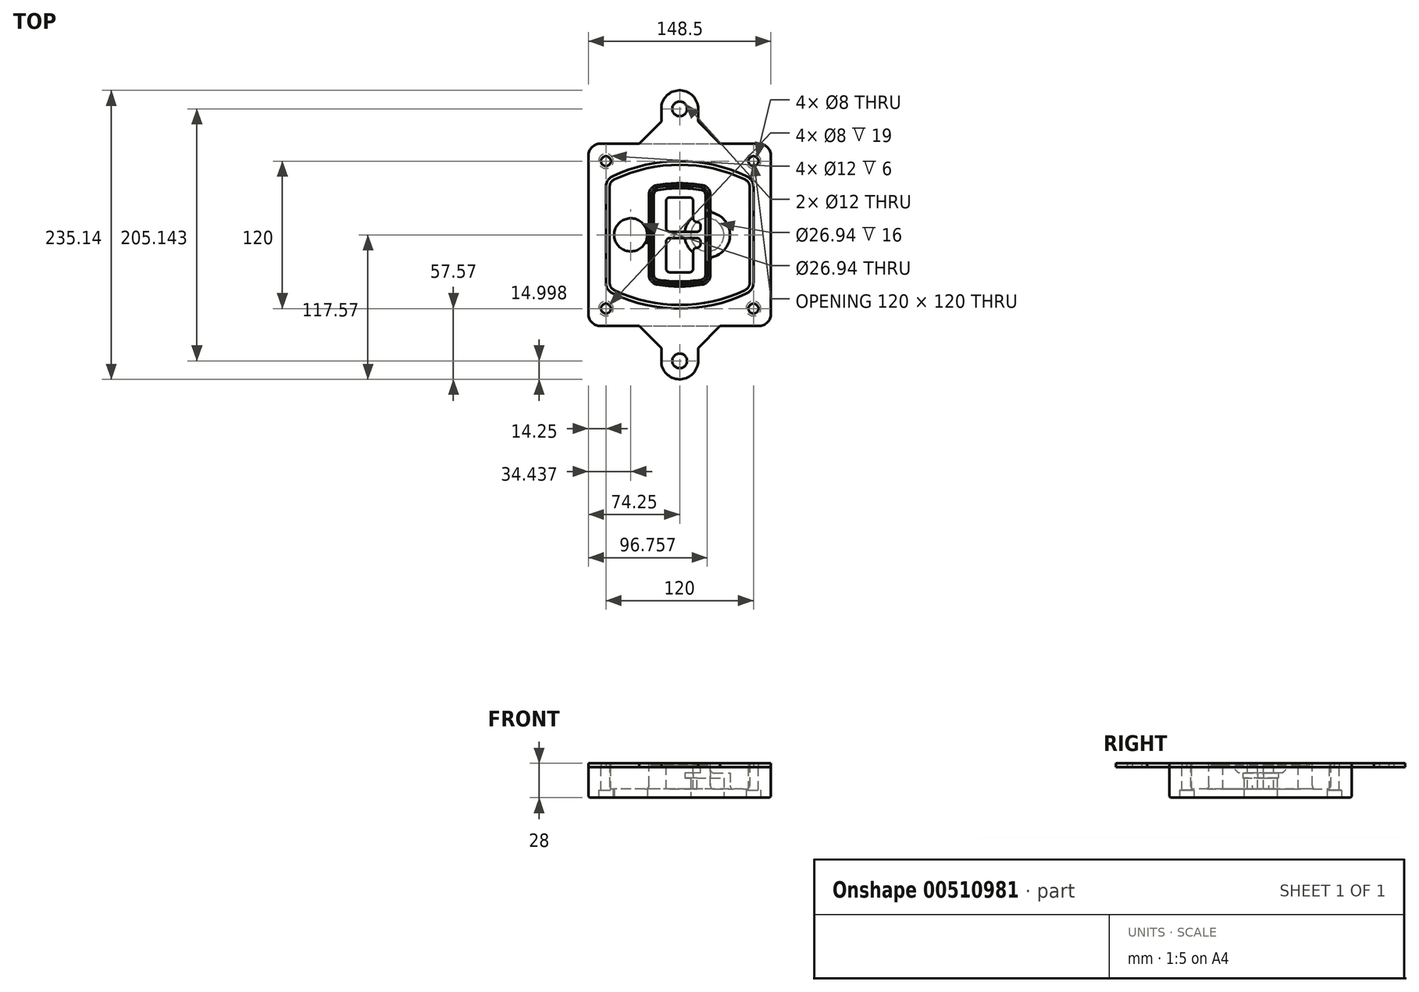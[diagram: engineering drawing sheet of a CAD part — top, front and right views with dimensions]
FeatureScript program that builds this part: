
annotation { "Feature Type Name" : "Feature", "Feature Type Description" : "" }
export const myFeature = defineFeature(function(context is Context, id is Id, definition is map)
    precondition{}
    {
        {
            var Q0;
            Q0=qCreatedBy(makeId("Top.planeOp"),FACE);
            var sketch = newSketch(context, id + "F0", { "sketchPlane" : qUnion([Q0])});
            skPoint(sketch, "E0.rect.middle", {"position": v(0, 0) * mm});
            skLineSegment(sketch, "E1.bottom", {"start": v(-64.25, -74.25) * mm, "end": v(64.25, -74.25) * mm});
            skLineSegment(sketch, "E1.top", {"start": v(-64.25, 74.25) * mm, "end": v(64.25, 74.25) * mm});
            skLineSegment(sketch, "E1.left", {"start": v(-74.25, -64.25) * mm, "end": v(-74.25, 64.25) * mm});
            skLineSegment(sketch, "E1.right", {"start": v(74.25, -64.25) * mm, "end": v(74.25, 64.25) * mm});
            skLineSegment(sketch, "E2", {"start": v(-74.25, 74.25) * mm, "end": v(74.25, -74.25) * mm, "construction": true});
            skLineSegment(sketch, "E3", {"start": v(74.25, 74.25) * mm, "end": v(-74.25, -74.25) * mm, "construction": true});
            skCircle(sketch, "E4", {"center": v(-60, 60) * mm, "radius": 4 * mm});
            skCircle(sketch, "E5", {"center": v(60, 60) * mm, "radius": 4 * mm});
            skCircle(sketch, "E6", {"center": v(60, -60) * mm, "radius": 4 * mm});
            skCircle(sketch, "E7", {"center": v(-60, -60) * mm, "radius": 4 * mm});
            skLineSegment(sketch, "E8", {"start": v(-60, 60) * mm, "end": v(60, 60) * mm, "construction": true});
            skLineSegment(sketch, "E9", {"start": v(60, 60) * mm, "end": v(60, -60) * mm, "construction": true});
            skLineSegment(sketch, "E10", {"start": v(60, -60) * mm, "end": v(-60, -60) * mm, "construction": true});
            skLineSegment(sketch, "E11", {"start": v(-60, -60) * mm, "end": v(-60, 60) * mm, "construction": true});
            skLineSegment(sketch, "E12", {"start": v(-60, 38.83) * mm, "end": v(-60, -38.83) * mm});
            skLineSegment(sketch, "E13", {"start": v(60, 38.83) * mm, "end": v(60, -38.83) * mm});
            skArc(sketch, "E14", {"start": v(54.26, 47.88) * mm, "mid": v(0, 60) * mm, "end": v(-54.26, 47.88) * mm});
            skArc(sketch, "E15", {"start": v(-54.26, -47.88) * mm, "mid": v(0, -60) * mm, "end": v(54.26, -47.88) * mm});
            skLineSegment(sketch, "E16", {"start": v(-60, 0) * mm, "end": v(60, 0) * mm, "construction": true});
            skPoint(sketch, "E17.visualSharp", {"position": v(-60, -45) * mm});
            skArc(sketch, "E17.filletArc", {"start": v(-60, -38.83) * mm, "mid": v(-58.44, -44.2) * mm, "end": v(-54.26, -47.88) * mm});
            skPoint(sketch, "E18.visualSharp", {"position": v(-60, 45) * mm});
            skArc(sketch, "E18.filletArc", {"start": v(-54.26, 47.88) * mm, "mid": v(-58.44, 44.2) * mm, "end": v(-60, 38.83) * mm});
            skPoint(sketch, "E19.visualSharp", {"position": v(60, 45) * mm});
            skArc(sketch, "E19.filletArc", {"start": v(60, 38.83) * mm, "mid": v(58.44, 44.2) * mm, "end": v(54.26, 47.88) * mm});
            skPoint(sketch, "E20.visualSharp", {"position": v(60, -45) * mm});
            skArc(sketch, "E20.filletArc", {"start": v(54.26, -47.88) * mm, "mid": v(58.44, -44.2) * mm, "end": v(60, -38.83) * mm});
            skPoint(sketch, "E21.visualSharp", {"position": v(-74.25, 74.25) * mm});
            skArc(sketch, "E21.filletArc", {"start": v(-64.25, 74.25) * mm, "mid": v(-71.32, 71.32) * mm, "end": v(-74.25, 64.25) * mm});
            skPoint(sketch, "E22.visualSharp", {"position": v(74.25, 74.25) * mm});
            skArc(sketch, "E22.filletArc", {"start": v(74.25, 64.25) * mm, "mid": v(71.32, 71.32) * mm, "end": v(64.25, 74.25) * mm});
            skPoint(sketch, "E23.visualSharp", {"position": v(74.25, -74.25) * mm});
            skArc(sketch, "E23.filletArc", {"start": v(64.25, -74.25) * mm, "mid": v(71.32, -71.32) * mm, "end": v(74.25, -64.25) * mm});
            skPoint(sketch, "E24.visualSharp", {"position": v(-74.25, -74.25) * mm});
            skArc(sketch, "E24.filletArc", {"start": v(-74.25, -64.25) * mm, "mid": v(-71.32, -71.32) * mm, "end": v(-64.25, -74.25) * mm});
            skArc(sketch, "E25.0", {"start": v(57, 38.83) * mm, "mid": v(55.9, 42.58) * mm, "end": v(52.98, 45.17) * mm});
            skLineSegment(sketch, "E25.1", {"start": v(57, 38.83) * mm, "end": v(57, -38.83) * mm});
            skArc(sketch, "E25.2", {"start": v(52.98, -45.17) * mm, "mid": v(55.9, -42.58) * mm, "end": v(57, -38.83) * mm});
            skArc(sketch, "E25.3", {"start": v(-52.98, -45.17) * mm, "mid": v(0, -57) * mm, "end": v(52.98, -45.17) * mm});
            skArc(sketch, "E25.4", {"start": v(-57, -38.83) * mm, "mid": v(-55.9, -42.58) * mm, "end": v(-52.98, -45.17) * mm});
            skArc(sketch, "E25.5", {"start": v(52.98, 45.17) * mm, "mid": v(0, 57) * mm, "end": v(-52.98, 45.17) * mm});
            skLineSegment(sketch, "E25.6", {"start": v(-57, 38.83) * mm, "end": v(-57, -38.83) * mm});
            skArc(sketch, "E25.7", {"start": v(-52.98, 45.17) * mm, "mid": v(-55.9, 42.58) * mm, "end": v(-57, 38.83) * mm});
            skArc(sketch, "E26.0", {"start": v(-55.96, 51.5) * mm, "mid": v(-61.82, 46.33) * mm, "end": v(-64, 38.83) * mm});
            skArc(sketch, "E26.1", {"start": v(55.96, 51.5) * mm, "mid": v(0, 64) * mm, "end": v(-55.96, 51.5) * mm});
            skArc(sketch, "E26.2", {"start": v(64, 38.83) * mm, "mid": v(61.82, 46.33) * mm, "end": v(55.96, 51.5) * mm});
            skLineSegment(sketch, "E26.3", {"start": v(64, 38.83) * mm, "end": v(64, -38.83) * mm});
            skArc(sketch, "E26.4", {"start": v(55.96, -51.5) * mm, "mid": v(61.82, -46.33) * mm, "end": v(64, -38.83) * mm});
            skLineSegment(sketch, "E26.5", {"start": v(-64, 38.83) * mm, "end": v(-64, -38.83) * mm});
            skArc(sketch, "E26.6", {"start": v(-55.96, -51.5) * mm, "mid": v(0, -64) * mm, "end": v(55.96, -51.5) * mm});
            skArc(sketch, "E26.7", {"start": v(-64, -38.83) * mm, "mid": v(-61.82, -46.33) * mm, "end": v(-55.96, -51.5) * mm});
            skSolve(sketch);
        }
        {
            var Q0;
            Q0=makeQuery(id+"F0.imprint","IMPRINT",FACE,{"disambiguationData":[TD([[makeQuery(id+"F0.imprint","IMPRINT",EDGE,{"derivedFrom":sQuery(id+"F0.wireOp",EDGE,"E1.bottom")}),1.0]])]});
            var Q1;
            Q1=makeQuery(id+"F0.imprint","IMPRINT",FACE,{"disambiguationData":[TD([[makeQuery(id+"F0.imprint","IMPRINT",EDGE,{"derivedFrom":sQuery(id+"F0.wireOp",EDGE,"E12")}),1.0]])]});
            var Q2;
            Q2=makeQuery(id+"F0.imprint","IMPRINT",FACE,{"disambiguationData":[TD([[makeQuery(id+"F0.imprint","IMPRINT",EDGE,{"derivedFrom":sQuery(id+"F0.wireOp",EDGE,"E25.0")}),1.0]])]});
            var Q3;
            Q3=makeQuery(id+"F0.imprint","IMPRINT",FACE,{"disambiguationData":[TD([[makeQuery(id+"F0.imprint","IMPRINT",EDGE,{"derivedFrom":sQuery(id+"F0.wireOp",EDGE,"E12")}),-1.0]])]});
            extrude(context, id + "F1", {"entities" : qUnion([Q0, Q1, Q2, Q3]), "oppositeDirection" : true, "depth" : 25 * mm});
        }
        {
            var Q0;
            Q0=makeQuery(id+"F0.imprint","IMPRINT",FACE,{"disambiguationData":[TD([[makeQuery(id+"F0.imprint","IMPRINT",EDGE,{"derivedFrom":sQuery(id+"F0.wireOp",EDGE,"E12")}),1.0]])]});
            extrude(context, id + "F2", {"entities" : qUnion([Q0]), "operationType" : NewBodyOperationType.ADD, "depth" : 3 * mm});
        }
        {
            var Q0;
            Q0=makeQuery(id+"F0.imprint","IMPRINT",FACE,{"disambiguationData":[TD([[makeQuery(id+"F0.imprint","IMPRINT",EDGE,{"derivedFrom":sQuery(id+"F0.wireOp",EDGE,"E25.0")}),1.0]])]});
            extrude(context, id + "F3", {"entities" : qUnion([Q0]), "operationType" : NewBodyOperationType.REMOVE, "oppositeDirection" : true, "depth" : 18 * mm});
        }
        {
            var Q0;
            Q0=makeQuery(id+"F2.opExtrude","CAP_FACE",FACE,{"disambiguationData":[OSD([sQuery(id+"F0.wireOp",EDGE,"E12"),sQuery(id+"F0.wireOp",EDGE,"E13"),sQuery(id+"F0.wireOp",EDGE,"E14"),sQuery(id+"F0.wireOp",EDGE,"E15"),sQuery(id+"F0.wireOp",EDGE,"E17.filletArc"),sQuery(id+"F0.wireOp",EDGE,"E18.filletArc"),sQuery(id+"F0.wireOp",EDGE,"E19.filletArc"),sQuery(id+"F0.wireOp",EDGE,"E20.filletArc"),sQuery(id+"F0.wireOp",EDGE,"E25.0"),sQuery(id+"F0.wireOp",EDGE,"E25.1"),sQuery(id+"F0.wireOp",EDGE,"E25.2"),sQuery(id+"F0.wireOp",EDGE,"E25.3"),sQuery(id+"F0.wireOp",EDGE,"E25.4"),sQuery(id+"F0.wireOp",EDGE,"E25.5"),sQuery(id+"F0.wireOp",EDGE,"E25.6"),sQuery(id+"F0.wireOp",EDGE,"E25.7")])],"isStart":false});
            var sketch = newSketch(context, id + "F4", { "sketchPlane" : qUnion([Q0])});
            skArc(sketch, "E27.0", {"start": v(-18.34, -40.45) * mm, "mid": v(0, -42) * mm, "end": v(18.34, -40.45) * mm});
            skArc(sketch, "E28.0", {"start": v(18.34, 40.45) * mm, "mid": v(0, 42) * mm, "end": v(-18.34, 40.45) * mm});
            skLineSegment(sketch, "E29", {"start": v(-25, 32.57) * mm, "end": v(-25, -32.57) * mm});
            skLineSegment(sketch, "E30", {"start": v(25, 32.57) * mm, "end": v(25, -32.57) * mm});
            skLineSegment(sketch, "E31", {"start": v(-25, 39.1) * mm, "end": v(25, 39.1) * mm, "construction": true});
            skLineSegment(sketch, "E32", {"start": v(-25, -39.1) * mm, "end": v(25, -39.1) * mm, "construction": true});
            skPoint(sketch, "E33.visualSharp", {"position": v(-25, 39.1) * mm});
            skArc(sketch, "E33.filletArc", {"start": v(-18.34, 40.45) * mm, "mid": v(-23.11, 37.73) * mm, "end": v(-25, 32.57) * mm});
            skPoint(sketch, "E34.visualSharp", {"position": v(25, 39.1) * mm});
            skArc(sketch, "E34.filletArc", {"start": v(25, 32.57) * mm, "mid": v(23.11, 37.73) * mm, "end": v(18.34, 40.45) * mm});
            skPoint(sketch, "E35.visualSharp", {"position": v(25, -39.1) * mm});
            skArc(sketch, "E35.filletArc", {"start": v(18.34, -40.45) * mm, "mid": v(23.11, -37.73) * mm, "end": v(25, -32.57) * mm});
            skPoint(sketch, "E36.visualSharp", {"position": v(-25, -39.1) * mm});
            skArc(sketch, "E36.filletArc", {"start": v(-25, -32.57) * mm, "mid": v(-23.11, -37.73) * mm, "end": v(-18.34, -40.45) * mm});
            skArc(sketch, "E37.0", {"start": v(52.98, 45.17) * mm, "mid": v(0, 57) * mm, "end": v(-52.98, 45.17) * mm});
            skArc(sketch, "E37.1", {"start": v(-52.98, 45.17) * mm, "mid": v(-55.9, 42.58) * mm, "end": v(-57, 38.83) * mm});
            skLineSegment(sketch, "E37.2", {"start": v(-57, 38.83) * mm, "end": v(-57, -38.83) * mm});
            skArc(sketch, "E37.3", {"start": v(-57, -38.83) * mm, "mid": v(-55.9, -42.58) * mm, "end": v(-52.98, -45.17) * mm});
            skArc(sketch, "E37.4", {"start": v(-52.98, -45.17) * mm, "mid": v(0, -57) * mm, "end": v(52.98, -45.17) * mm});
            skArc(sketch, "E37.5", {"start": v(52.98, -45.17) * mm, "mid": v(55.9, -42.58) * mm, "end": v(57, -38.83) * mm});
            skLineSegment(sketch, "E37.6", {"start": v(57, 38.83) * mm, "end": v(57, -38.83) * mm});
            skArc(sketch, "E37.7", {"start": v(57, 38.83) * mm, "mid": v(55.9, 42.58) * mm, "end": v(52.98, 45.17) * mm});
            skLineSegment(sketch, "E38.0", {"start": v(23, 32.57) * mm, "end": v(23, -32.57) * mm});
            skArc(sketch, "E38.1", {"start": v(18, -38.48) * mm, "mid": v(21.58, -36.44) * mm, "end": v(23, -32.57) * mm});
            skArc(sketch, "E38.2", {"start": v(-18, -38.48) * mm, "mid": v(0, -40) * mm, "end": v(18, -38.48) * mm});
            skArc(sketch, "E38.3", {"start": v(-23, -32.57) * mm, "mid": v(-21.58, -36.44) * mm, "end": v(-18, -38.48) * mm});
            skLineSegment(sketch, "E38.4", {"start": v(-23, 32.57) * mm, "end": v(-23, -32.57) * mm});
            skArc(sketch, "E38.5", {"start": v(23, 32.57) * mm, "mid": v(21.58, 36.44) * mm, "end": v(18, 38.48) * mm});
            skArc(sketch, "E38.6", {"start": v(-18, 38.48) * mm, "mid": v(-21.58, 36.44) * mm, "end": v(-23, 32.57) * mm});
            skArc(sketch, "E38.7", {"start": v(18, 38.48) * mm, "mid": v(0, 40) * mm, "end": v(-18, 38.48) * mm});
            skArc(sketch, "E39.0", {"start": v(21, 32.57) * mm, "mid": v(20.06, 35.15) * mm, "end": v(17.67, 36.5) * mm});
            skLineSegment(sketch, "E39.1", {"start": v(21, 32.57) * mm, "end": v(21, -32.57) * mm});
            skArc(sketch, "E39.2", {"start": v(17.67, -36.5) * mm, "mid": v(20.06, -35.15) * mm, "end": v(21, -32.57) * mm});
            skArc(sketch, "E39.3", {"start": v(-17.67, -36.5) * mm, "mid": v(0, -38) * mm, "end": v(17.67, -36.5) * mm});
            skArc(sketch, "E39.4", {"start": v(-21, -32.57) * mm, "mid": v(-20.06, -35.15) * mm, "end": v(-17.67, -36.5) * mm});
            skArc(sketch, "E39.5", {"start": v(17.67, 36.5) * mm, "mid": v(0, 38) * mm, "end": v(-17.67, 36.5) * mm});
            skLineSegment(sketch, "E39.6", {"start": v(-21, 32.57) * mm, "end": v(-21, -32.57) * mm});
            skArc(sketch, "E39.7", {"start": v(-17.67, 36.5) * mm, "mid": v(-20.06, 35.15) * mm, "end": v(-21, 32.57) * mm});
            skLineSegment(sketch, "E40", {"start": v(-25, 0) * mm, "end": v(25, 0) * mm, "construction": true});
            skLineSegment(sketch, "E41", {"start": v(-11, 5.5) * mm, "end": v(-11, 27.5) * mm});
            skLineSegment(sketch, "E42", {"start": v(-8, 30.5) * mm, "end": v(8, 30.5) * mm});
            skLineSegment(sketch, "E43", {"start": v(11, 27.5) * mm, "end": v(11, 13.5) * mm});
            skLineSegment(sketch, "E44", {"start": v(14, 10.5) * mm, "end": v(14, 10.5) * mm});
            skLineSegment(sketch, "E45", {"start": v(17, 7.5) * mm, "end": v(17, 5.5) * mm});
            skLineSegment(sketch, "E46", {"start": v(14, 2.5) * mm, "end": v(-8, 2.5) * mm});
            skPoint(sketch, "E47.visualSharp", {"position": v(-11, 30.5) * mm});
            skArc(sketch, "E47.filletArc", {"start": v(-8, 30.5) * mm, "mid": v(-10.12, 29.62) * mm, "end": v(-11, 27.5) * mm});
            skPoint(sketch, "E48.visualSharp", {"position": v(11, 30.5) * mm});
            skArc(sketch, "E48.filletArc", {"start": v(11, 27.5) * mm, "mid": v(10.12, 29.62) * mm, "end": v(8, 30.5) * mm});
            skPoint(sketch, "E49.visualSharp", {"position": v(11, 10.5) * mm});
            skArc(sketch, "E49.filletArc", {"start": v(11, 13.5) * mm, "mid": v(11.88, 11.38) * mm, "end": v(14, 10.5) * mm});
            skPoint(sketch, "E50.visualSharp", {"position": v(17, 10.5) * mm});
            skArc(sketch, "E50.filletArc", {"start": v(17, 7.5) * mm, "mid": v(16.12, 9.62) * mm, "end": v(14, 10.5) * mm});
            skPoint(sketch, "E51.visualSharp", {"position": v(17, 2.5) * mm});
            skArc(sketch, "E51.filletArc", {"start": v(14, 2.5) * mm, "mid": v(16.12, 3.38) * mm, "end": v(17, 5.5) * mm});
            skPoint(sketch, "E52.visualSharp", {"position": v(-11, 2.5) * mm});
            skArc(sketch, "E52.filletArc", {"start": v(-11, 5.5) * mm, "mid": v(-10.12, 3.38) * mm, "end": v(-8, 2.5) * mm});
            skLineSegment(sketch, "E53.0.MirrorCS", {"start": v(14, -2.5) * mm, "end": v(-8, -2.5) * mm});
            skArc(sketch, "E54.0.MirrorCS", {"start": v(-11, -5.5) * mm, "mid": v(-10.12, -3.38) * mm, "end": v(-8, -2.5) * mm});
            skLineSegment(sketch, "E55.0.MirrorCS", {"start": v(-11, -5.5) * mm, "end": v(-11, -27.5) * mm});
            skArc(sketch, "E56.0.MirrorCS", {"start": v(-8, -30.5) * mm, "mid": v(-10.12, -29.62) * mm, "end": v(-11, -27.5) * mm});
            skLineSegment(sketch, "E57.0.MirrorCS", {"start": v(-8, -30.5) * mm, "end": v(8, -30.5) * mm});
            skArc(sketch, "E58.0.MirrorCS", {"start": v(11, -27.5) * mm, "mid": v(10.12, -29.62) * mm, "end": v(8, -30.5) * mm});
            skLineSegment(sketch, "E59.0.MirrorCS", {"start": v(11, -27.5) * mm, "end": v(11, -13.5) * mm});
            skArc(sketch, "E60.0.MirrorCS", {"start": v(11, -13.5) * mm, "mid": v(11.88, -11.38) * mm, "end": v(14, -10.5) * mm});
            skArc(sketch, "E61.0.MirrorCS", {"start": v(17, -7.5) * mm, "mid": v(16.12, -9.62) * mm, "end": v(14, -10.5) * mm});
            skLineSegment(sketch, "E62.0.MirrorCS", {"start": v(17, -7.5) * mm, "end": v(17, -5.5) * mm});
            skArc(sketch, "E63.0.MirrorCS", {"start": v(14, -2.5) * mm, "mid": v(16.12, -3.38) * mm, "end": v(17, -5.5) * mm});
            skSolve(sketch);
        }
        {
            var Q0;
            Q0=makeQuery(id+"F4.imprint","IMPRINT",FACE,{"disambiguationData":[TD([[makeQuery(id+"F4.imprint","IMPRINT",EDGE,{"derivedFrom":sQuery(id+"F4.wireOp",EDGE,"E27.0")}),1.0]])]});
            var Q1;
            Q1=makeQuery(id+"F4.imprint","IMPRINT",FACE,{"disambiguationData":[TD([[makeQuery(id+"F4.imprint","IMPRINT",EDGE,{"derivedFrom":sQuery(id+"F4.wireOp",EDGE,"E38.0")}),-1.0]])]});
            var Q2;
            Q2=makeQuery(id+"F4.imprint","IMPRINT",FACE,{"disambiguationData":[TD([[makeQuery(id+"F4.imprint","IMPRINT",EDGE,{"derivedFrom":sQuery(id+"F4.wireOp",EDGE,"E39.0")}),1.0]])]});
            extrude(context, id + "F5", {"entities" : qUnion([Q0, Q1, Q2]), "operationType" : NewBodyOperationType.ADD, "endBound" : BoundingType.UP_TO_NEXT, "oppositeDirection" : true, "depth" : 25 * mm});
        }
        {
            var Q0;
            Q0=makeQuery(id+"F4.imprint","IMPRINT",FACE,{"disambiguationData":[TD([[makeQuery(id+"F4.imprint","IMPRINT",EDGE,{"derivedFrom":sQuery(id+"F4.wireOp",EDGE,"E38.0")}),-1.0]])]});
            extrude(context, id + "F6", {"entities" : qUnion([Q0]), "operationType" : NewBodyOperationType.REMOVE, "oppositeDirection" : true, "depth" : 2 * mm});
        }
        {
            var Q0;
            Q0=makeQuery(id+"F1.opExtrude","CAP_FACE",FACE,{"disambiguationData":[OSD([sQuery(id+"F0.wireOp",EDGE,"E1.bottom"),sQuery(id+"F0.wireOp",EDGE,"E1.top"),sQuery(id+"F0.wireOp",EDGE,"E1.left"),sQuery(id+"F0.wireOp",EDGE,"E1.right"),sQuery(id+"F0.wireOp",EDGE,"E4"),sQuery(id+"F0.wireOp",EDGE,"E5"),sQuery(id+"F0.wireOp",EDGE,"E6"),sQuery(id+"F0.wireOp",EDGE,"E7"),sQuery(id+"F0.wireOp",EDGE,"E21.filletArc"),sQuery(id+"F0.wireOp",EDGE,"E22.filletArc"),sQuery(id+"F0.wireOp",EDGE,"E23.filletArc"),sQuery(id+"F0.wireOp",EDGE,"E24.filletArc")])],"isStart":false});
            var sketch = newSketch(context, id + "F7", { "sketchPlane" : qUnion([Q0])});
            skCircle(sketch, "E64", {"center": v(22.5, 0) * mm, "radius": 13.47 * mm});
            skCircle(sketch, "E65", {"center": v(-39.81, 0) * mm, "radius": 13.47 * mm});
            skLineSegment(sketch, "E66", {"start": v(74.25, 0) * mm, "end": v(-74.25, 0) * mm});
            skCircle(sketch, "E67", {"center": v(22.5, 0) * mm, "radius": 18.47 * mm});
            skCircle(sketch, "E68", {"center": v(60, -60) * mm, "radius": 6 * mm});
            skCircle(sketch, "E69", {"center": v(-60, -60) * mm, "radius": 6 * mm});
            skCircle(sketch, "E70", {"center": v(-60, 60) * mm, "radius": 6 * mm});
            skCircle(sketch, "E71", {"center": v(60, 60) * mm, "radius": 6 * mm});
            skSolve(sketch);
        }
        {
            var Q0;
            {var subQ1=sQuery(id+"F7.wireOp",EDGE,"E66");var subQ4=sQuery(id+"F7.wireOp",EDGE,"E64");var subQ6=makeQuery(id+"F7.imprint","INTERSECT",VERTEX,{"disambiguationData":[OD(0.0)],"derivedFrom":[subQ4,subQ1]});Q0=makeQuery(id+"F7.imprint","IMPRINT",FACE,{"disambiguationData":[TD([[makeQuery(id+"F7.imprint","IMPRINT",EDGE,{"disambiguationData":[TD([[subQ6,-1.0]])],"derivedFrom":subQ4}),-1.0]])]});}
            var Q1;
            {var subQ0=sQuery(id+"F7.wireOp",EDGE,"E66");var subQ1=sQuery(id+"F7.wireOp",EDGE,"E64");var subQ3=makeQuery(id+"F7.imprint","INTERSECT",VERTEX,{"disambiguationData":[OD(0.0)],"derivedFrom":[subQ1,subQ0]});Q1=makeQuery(id+"F7.imprint","IMPRINT",FACE,{"disambiguationData":[TD([[makeQuery(id+"F7.imprint","IMPRINT",EDGE,{"disambiguationData":[TD([[subQ3,-1.0]])],"derivedFrom":subQ1}),1.0]])]});}
            var Q2;
            {var subQ0=sQuery(id+"F7.wireOp",EDGE,"E66");var subQ1=sQuery(id+"F7.wireOp",EDGE,"E64");var subQ3=makeQuery(id+"F7.imprint","INTERSECT",VERTEX,{"disambiguationData":[OD(0.0)],"derivedFrom":[subQ1,subQ0]});Q2=makeQuery(id+"F7.imprint","IMPRINT",FACE,{"disambiguationData":[TD([[makeQuery(id+"F7.imprint","IMPRINT",EDGE,{"disambiguationData":[TD([[subQ3,1.0]])],"derivedFrom":subQ1}),1.0]])]});}
            var Q3;
            {var subQ1=sQuery(id+"F7.wireOp",EDGE,"E66");var subQ4=sQuery(id+"F7.wireOp",EDGE,"E64");var subQ6=makeQuery(id+"F7.imprint","INTERSECT",VERTEX,{"disambiguationData":[OD(0.0)],"derivedFrom":[subQ4,subQ1]});Q3=makeQuery(id+"F7.imprint","IMPRINT",FACE,{"disambiguationData":[TD([[makeQuery(id+"F7.imprint","IMPRINT",EDGE,{"disambiguationData":[TD([[subQ6,1.0]])],"derivedFrom":subQ4}),-1.0]])]});}
            extrude(context, id + "F8", {"entities" : qUnion([Q0, Q1, Q2, Q3]), "operationType" : NewBodyOperationType.ADD, "oppositeDirection" : true, "depth" : 20 * mm});
        }
        {
            var Q0;
            {var subQ0=sQuery(id+"F7.wireOp",EDGE,"E66");var subQ1=sQuery(id+"F7.wireOp",EDGE,"E64");var subQ3=makeQuery(id+"F7.imprint","INTERSECT",VERTEX,{"disambiguationData":[OD(0.0)],"derivedFrom":[subQ1,subQ0]});Q0=makeQuery(id+"F7.imprint","IMPRINT",FACE,{"disambiguationData":[TD([[makeQuery(id+"F7.imprint","IMPRINT",EDGE,{"disambiguationData":[TD([[subQ3,-1.0]])],"derivedFrom":subQ1}),1.0]])]});}
            var Q1;
            {var subQ0=sQuery(id+"F7.wireOp",EDGE,"E66");var subQ1=sQuery(id+"F7.wireOp",EDGE,"E64");var subQ3=makeQuery(id+"F7.imprint","INTERSECT",VERTEX,{"disambiguationData":[OD(0.0)],"derivedFrom":[subQ1,subQ0]});Q1=makeQuery(id+"F7.imprint","IMPRINT",FACE,{"disambiguationData":[TD([[makeQuery(id+"F7.imprint","IMPRINT",EDGE,{"disambiguationData":[TD([[subQ3,1.0]])],"derivedFrom":subQ1}),1.0]])]});}
            extrude(context, id + "F9", {"entities" : qUnion([Q0, Q1]), "operationType" : NewBodyOperationType.REMOVE, "oppositeDirection" : true, "depth" : 16 * mm});
        }
        {
            var Q0;
            {var subQ0=sQuery(id+"F7.wireOp",EDGE,"E66");var subQ1=sQuery(id+"F7.wireOp",EDGE,"E65");var subQ3=makeQuery(id+"F7.imprint","INTERSECT",VERTEX,{"disambiguationData":[OD(0.0)],"derivedFrom":[subQ1,subQ0]});Q0=makeQuery(id+"F7.imprint","IMPRINT",FACE,{"disambiguationData":[TD([[makeQuery(id+"F7.imprint","IMPRINT",EDGE,{"disambiguationData":[TD([[subQ3,-1.0]])],"derivedFrom":subQ1}),1.0]])]});}
            var Q1;
            {var subQ0=sQuery(id+"F7.wireOp",EDGE,"E66");var subQ1=sQuery(id+"F7.wireOp",EDGE,"E65");var subQ3=makeQuery(id+"F7.imprint","INTERSECT",VERTEX,{"disambiguationData":[OD(0.0)],"derivedFrom":[subQ1,subQ0]});Q1=makeQuery(id+"F7.imprint","IMPRINT",FACE,{"disambiguationData":[TD([[makeQuery(id+"F7.imprint","IMPRINT",EDGE,{"disambiguationData":[TD([[subQ3,1.0]])],"derivedFrom":subQ1}),1.0]])]});}
            extrude(context, id + "F10", {"entities" : qUnion([Q0, Q1]), "operationType" : NewBodyOperationType.REMOVE, "oppositeDirection" : true, "depth" : 25 * mm});
        }
        {
            var Q0;
            Q0=makeQuery(id+"F7.imprint","IMPRINT",FACE,{"disambiguationData":[TD([[makeQuery(id+"F7.imprint","IMPRINT",EDGE,{"derivedFrom":sQuery(id+"F7.wireOp",EDGE,"E68")}),1.0]])]});
            var Q1;
            Q1=makeQuery(id+"F7.imprint","IMPRINT",FACE,{"disambiguationData":[TD([[makeQuery(id+"F7.imprint","IMPRINT",EDGE,{"derivedFrom":makeQuery(id+"F1.opExtrude","CAP_EDGE",EDGE,{"disambiguationData":[OSD([sQuery(id+"F0.wireOp",EDGE,"E5")])],"isStart":false})}),-1.0]])]});
            var Q2;
            Q2=makeQuery(id+"F7.imprint","IMPRINT",FACE,{"disambiguationData":[TD([[makeQuery(id+"F7.imprint","IMPRINT",EDGE,{"derivedFrom":sQuery(id+"F7.wireOp",EDGE,"E69")}),1.0]])]});
            var Q3;
            Q3=makeQuery(id+"F7.imprint","IMPRINT",FACE,{"disambiguationData":[TD([[makeQuery(id+"F7.imprint","IMPRINT",EDGE,{"derivedFrom":makeQuery(id+"F1.opExtrude","CAP_EDGE",EDGE,{"disambiguationData":[OSD([sQuery(id+"F0.wireOp",EDGE,"E4")])],"isStart":false})}),-1.0]])]});
            var Q4;
            Q4=makeQuery(id+"F7.imprint","IMPRINT",FACE,{"disambiguationData":[TD([[makeQuery(id+"F7.imprint","IMPRINT",EDGE,{"derivedFrom":sQuery(id+"F7.wireOp",EDGE,"E70")}),1.0]])]});
            var Q5;
            Q5=makeQuery(id+"F7.imprint","IMPRINT",FACE,{"disambiguationData":[TD([[makeQuery(id+"F7.imprint","IMPRINT",EDGE,{"derivedFrom":makeQuery(id+"F1.opExtrude","CAP_EDGE",EDGE,{"disambiguationData":[OSD([sQuery(id+"F0.wireOp",EDGE,"E7")])],"isStart":false})}),-1.0]])]});
            var Q6;
            Q6=makeQuery(id+"F7.imprint","IMPRINT",FACE,{"disambiguationData":[TD([[makeQuery(id+"F7.imprint","IMPRINT",EDGE,{"derivedFrom":sQuery(id+"F7.wireOp",EDGE,"E71")}),1.0]])]});
            var Q7;
            Q7=makeQuery(id+"F7.imprint","IMPRINT",FACE,{"disambiguationData":[TD([[makeQuery(id+"F7.imprint","IMPRINT",EDGE,{"derivedFrom":makeQuery(id+"F1.opExtrude","CAP_EDGE",EDGE,{"disambiguationData":[OSD([sQuery(id+"F0.wireOp",EDGE,"E6")])],"isStart":false})}),-1.0]])]});
            extrude(context, id + "F11", {"entities" : qUnion([Q0, Q1, Q2, Q3, Q4, Q5, Q6, Q7]), "operationType" : NewBodyOperationType.REMOVE, "oppositeDirection" : true, "depth" : 6 * mm});
        }
        {
            var Q0;
            Q0=makeQuery(id+"F9.boolean.opBoolean","COPY",FACE,{"derivedFrom":makeQuery(id+"F9.opExtrude","CAP_FACE",FACE,{"disambiguationData":[OSD([sQuery(id+"F7.wireOp",EDGE,"E64")])],"isStart":false})});
            var sketch = newSketch(context, id + "F12", { "sketchPlane" : qUnion([Q0])});
            skArc(sketch, "E72.0", {"start": v(11, 14.45) * mm, "mid": v(6.45, 9.13) * mm, "end": v(4.2, 2.5) * mm});
            skArc(sketch, "E72.1", {"start": v(4.2, -2.5) * mm, "mid": v(6.45, -9.13) * mm, "end": v(11, -14.45) * mm});
            skLineSegment(sketch, "E73", {"start": v(4.2, -2.5) * mm, "end": v(14, -2.5) * mm});
            skLineSegment(sketch, "E74.0", {"start": v(14, 2.5) * mm, "end": v(4.2, 2.5) * mm});
            skArc(sketch, "E74.1", {"start": v(14, 2.5) * mm, "mid": v(16.12, 3.38) * mm, "end": v(17, 5.5) * mm});
            skLineSegment(sketch, "E74.2", {"start": v(17, 7.5) * mm, "end": v(17, 5.5) * mm});
            skArc(sketch, "E74.3", {"start": v(17, 7.5) * mm, "mid": v(16.12, 9.62) * mm, "end": v(14, 10.5) * mm});
            skArc(sketch, "E74.4", {"start": v(11, 13.5) * mm, "mid": v(11.88, 11.38) * mm, "end": v(14, 10.5) * mm});
            skLineSegment(sketch, "E74.5", {"start": v(11, 14.45) * mm, "end": v(11, 13.5) * mm});
            skLineSegment(sketch, "E74.7", {"start": v(14, -2.5) * mm, "end": v(4.2, -2.5) * mm});
            skArc(sketch, "E74.8", {"start": v(14, -2.5) * mm, "mid": v(16.12, -3.38) * mm, "end": v(17, -5.5) * mm});
            skLineSegment(sketch, "E74.9", {"start": v(17, -7.5) * mm, "end": v(17, -5.5) * mm});
            skArc(sketch, "E74.10", {"start": v(17, -7.5) * mm, "mid": v(16.12, -9.62) * mm, "end": v(14, -10.5) * mm});
            skArc(sketch, "E74.11", {"start": v(11, -13.5) * mm, "mid": v(11.88, -11.38) * mm, "end": v(14, -10.5) * mm});
            skLineSegment(sketch, "E74.12", {"start": v(11, -14.45) * mm, "end": v(11, -13.5) * mm});
            skPoint(sketch, "E75.orphan", {"position": v(11, -27.5) * mm});
            skPoint(sketch, "E76.orphan", {"position": v(-8, -2.5) * mm});
            skPoint(sketch, "E77.orphan", {"position": v(-8, 2.5) * mm});
            skPoint(sketch, "E78.orphan", {"position": v(11, 27.5) * mm});
            skSolve(sketch);
        }
        {
            var Q0;
            {var subQ7=sQuery(id+"F12.wireOp",EDGE,"E72.0");var subQ14=sQuery(id+"F12.wireOp",EDGE,"E72.1");var subQ16=sQuery(id+"F12.wireOp",EDGE,"E74.1");var subQ18=sQuery(id+"F12.wireOp",EDGE,"E74.8");Q0=qUnion([makeQuery(id+"F12.imprint","IMPRINT",FACE,{"disambiguationData":[TD([[makeQuery(id+"F12.imprint","IMPRINT",EDGE,{"derivedFrom":subQ7}),1.0]])]}),makeQuery(id+"F12.imprint","IMPRINT",FACE,{"disambiguationData":[TD([[makeQuery(id+"F12.imprint","IMPRINT",EDGE,{"derivedFrom":subQ14}),1.0]])]}),makeQuery(id+"F12.imprint","IMPRINT",FACE,{"disambiguationData":[TD([[makeQuery(id+"F12.imprint","IMPRINT",EDGE,{"derivedFrom":subQ16}),1.0]])]}),makeQuery(id+"F12.imprint","IMPRINT",FACE,{"disambiguationData":[TD([[makeQuery(id+"F12.imprint","IMPRINT",EDGE,{"derivedFrom":subQ18}),-1.0]])]})]);}
            var Q1;
            Q1=makeQuery(id+"F5.boolean.opBoolean","SPLIT",FACE,{"disambiguationData":[TD([makeQuery(id+"F5.opExtrude","SWEPT_FACE",FACE,{"disambiguationData":[OSD([sQuery(id+"F4.wireOp",EDGE,"E41")])]})])],"derivedFrom":makeQuery(id+"F3.boolean.opBoolean","COPY",FACE,{"derivedFrom":makeQuery(id+"F3.opExtrude","CAP_FACE",FACE,{"disambiguationData":[OSD([sQuery(id+"F0.wireOp",EDGE,"E25.0"),sQuery(id+"F0.wireOp",EDGE,"E25.1"),sQuery(id+"F0.wireOp",EDGE,"E25.2"),sQuery(id+"F0.wireOp",EDGE,"E25.3"),sQuery(id+"F0.wireOp",EDGE,"E25.4"),sQuery(id+"F0.wireOp",EDGE,"E25.5"),sQuery(id+"F0.wireOp",EDGE,"E25.6"),sQuery(id+"F0.wireOp",EDGE,"E25.7")])],"isStart":false})})});
            extrude(context, id + "F13", {"entities" : qUnion([Q0]), "operationType" : NewBodyOperationType.REMOVE, "endBound" : BoundingType.UP_TO_SURFACE, "endBoundEntityFace" : qUnion([Q1]), "depth" : 25 * mm});
        }
        {
            var Q0;
            Q0=makeQuery(id+"F3.boolean.opBoolean","COPY",EDGE,{"derivedFrom":makeQuery(id+"F3.opExtrude","CAP_EDGE",EDGE,{"disambiguationData":[OSD([sQuery(id+"F0.wireOp",EDGE,"E25.6")])],"isStart":false})});
            var Q1;
            Q1=makeQuery(id+"F8.boolean.opBoolean","INTERSECT",EDGE,{"derivedFrom":[makeQuery(id+"F5.opExtrude","SWEPT_FACE",FACE,{"disambiguationData":[OSD([sQuery(id+"F4.wireOp",EDGE,"E30")])]}),makeQuery(id+"F8.opExtrude","CAP_FACE",FACE,{"disambiguationData":[OSD([sQuery(id+"F7.wireOp",EDGE,"E67")])],"isStart":false})]});
            var Q2;
            Q2=makeQuery(id+"F8.boolean.opBoolean","INTERSECT",EDGE,{"disambiguationData":[OD(1.0)],"derivedFrom":[makeQuery(id+"F5.opExtrude","SWEPT_FACE",FACE,{"disambiguationData":[OSD([sQuery(id+"F4.wireOp",EDGE,"E30")])]}),makeQuery(id+"F8.opExtrude","SWEPT_FACE",FACE,{"disambiguationData":[OSD([sQuery(id+"F7.wireOp",EDGE,"E67")])]})]});
            var Q3;
            {var subQ0=sQuery(id+"F4.wireOp",EDGE,"E30");Q3=makeQuery(id+"F8.boolean.opBoolean","SPLIT",EDGE,{"disambiguationData":[TD([makeQuery(id+"F5.opExtrude","SWEPT_FACE",FACE,{"disambiguationData":[OSD([sQuery(id+"F4.wireOp",EDGE,"E35.filletArc")])]})])],"derivedFrom":makeQuery(id+"F5.opExtrude","CAP_EDGE",EDGE,{"disambiguationData":[OSD([subQ0])],"isStart":false})});}
            var Q4;
            {var subQ0=sQuery(id+"F0.wireOp",EDGE,"E25.7");var subQ1=sQuery(id+"F0.wireOp",EDGE,"E25.1");var subQ2=sQuery(id+"F0.wireOp",EDGE,"E25.6");var subQ3=sQuery(id+"F0.wireOp",EDGE,"E25.5");var subQ4=sQuery(id+"F0.wireOp",EDGE,"E25.4");var subQ5=sQuery(id+"F0.wireOp",EDGE,"E25.0");var subQ6=sQuery(id+"F0.wireOp",EDGE,"E25.2");var subQ7=sQuery(id+"F0.wireOp",EDGE,"E25.3");Q4=makeQuery(id+"F8.boolean.opBoolean","INTERSECT",EDGE,{"derivedFrom":[makeQuery(id+"F5.boolean.opBoolean","SPLIT",FACE,{"disambiguationData":[TD([makeQuery(id+"F2.opExtrude","SWEPT_FACE",FACE,{"disambiguationData":[OSD([subQ5])]})])],"derivedFrom":makeQuery(id+"F3.boolean.opBoolean","COPY",FACE,{"derivedFrom":makeQuery(id+"F3.opExtrude","CAP_FACE",FACE,{"disambiguationData":[OSD([subQ5,subQ1,subQ6,subQ7,subQ4,subQ3,subQ2,subQ0])],"isStart":false})})}),makeQuery(id+"F8.opExtrude","SWEPT_FACE",FACE,{"disambiguationData":[OSD([sQuery(id+"F7.wireOp",EDGE,"E67")])]})]});}
            var Q5;
            Q5=makeQuery(id+"F8.boolean.opBoolean","INTERSECT",EDGE,{"disambiguationData":[OD(0.0)],"derivedFrom":[makeQuery(id+"F5.opExtrude","SWEPT_FACE",FACE,{"disambiguationData":[OSD([sQuery(id+"F4.wireOp",EDGE,"E30")])]}),makeQuery(id+"F8.opExtrude","SWEPT_FACE",FACE,{"disambiguationData":[OSD([sQuery(id+"F7.wireOp",EDGE,"E67")])]})]});
            fillet(context, id + "F14", {"entities" : qUnion([Q0, Q1, Q2, Q3, Q4, Q5]), "radius" : 3 * mm, "tangentPropagation" : true, "allowEdgeOverflow" : false});
        }
        {
            var Q0;
            Q0=makeQuery(id+"F1.opExtrude","CAP_EDGE",EDGE,{"disambiguationData":[OSD([sQuery(id+"F0.wireOp",EDGE,"E1.bottom")])],"isStart":false});
            fillet(context, id + "F15", {"entities" : qUnion([Q0]), "radius" : 2 * mm, "tangentPropagation" : true, "allowEdgeOverflow" : false});
        }
        {
            var Q0;
            {var subQ0=sQuery(id+"F0.wireOp",EDGE,"E21.filletArc");var subQ1=sQuery(id+"F0.wireOp",EDGE,"E7");var subQ2=sQuery(id+"F0.wireOp",EDGE,"E6");var subQ3=sQuery(id+"F0.wireOp",EDGE,"E5");var subQ4=sQuery(id+"F0.wireOp",EDGE,"E4");var subQ5=sQuery(id+"F0.wireOp",EDGE,"E22.filletArc");var subQ6=sQuery(id+"F0.wireOp",EDGE,"E1.bottom");var subQ7=sQuery(id+"F0.wireOp",EDGE,"E1.right");var subQ8=sQuery(id+"F0.wireOp",EDGE,"E1.top");var subQ9=sQuery(id+"F0.wireOp",EDGE,"E1.left");var subQ10=sQuery(id+"F0.wireOp",EDGE,"E23.filletArc");var subQ11=sQuery(id+"F0.wireOp",EDGE,"E24.filletArc");Q0=makeQuery(id+"F2.boolean.opBoolean","SPLIT",FACE,{"disambiguationData":[TD([makeQuery(id+"F1.opExtrude","SWEPT_FACE",FACE,{"disambiguationData":[OSD([subQ6])]})])],"derivedFrom":makeQuery(id+"F1.opExtrude","CAP_FACE",FACE,{"disambiguationData":[OSD([subQ6,subQ8,subQ9,subQ7,subQ4,subQ3,subQ2,subQ1,subQ0,subQ5,subQ10,subQ11])],"isStart":true})});}
            var sketch = newSketch(context, id + "F16", { "sketchPlane" : qUnion([Q0])});
            skArc(sketch, "E79.0", {"start": v(54.26, 47.88) * mm, "mid": v(0, 60) * mm, "end": v(-54.26, 47.88) * mm});
            skLineSegment(sketch, "E79.1", {"start": v(-64.25, 74.25) * mm, "end": v(64.25, 74.25) * mm});
            skArc(sketch, "E79.2", {"start": v(-64.25, 74.25) * mm, "mid": v(-71.32, 71.32) * mm, "end": v(-74.25, 64.25) * mm});
            skLineSegment(sketch, "E79.3", {"start": v(-74.25, -64.25) * mm, "end": v(-74.25, 64.25) * mm});
            skArc(sketch, "E79.4", {"start": v(-74.25, -64.25) * mm, "mid": v(-71.32, -71.32) * mm, "end": v(-64.25, -74.25) * mm});
            skLineSegment(sketch, "E79.5", {"start": v(-64.25, -74.25) * mm, "end": v(64.25, -74.25) * mm});
            skArc(sketch, "E79.6", {"start": v(64.25, -74.25) * mm, "mid": v(71.32, -71.32) * mm, "end": v(74.25, -64.25) * mm});
            skLineSegment(sketch, "E79.7", {"start": v(74.25, -64.25) * mm, "end": v(74.25, 64.25) * mm});
            skArc(sketch, "E79.8", {"start": v(74.25, 64.25) * mm, "mid": v(71.32, 71.32) * mm, "end": v(64.25, 74.25) * mm});
            skLineSegment(sketch, "E79.9", {"start": v(60, 38.83) * mm, "end": v(60, -38.83) * mm});
            skArc(sketch, "E79.10", {"start": v(-54.26, -47.88) * mm, "mid": v(0, -60) * mm, "end": v(54.26, -47.88) * mm});
            skArc(sketch, "E79.11", {"start": v(54.26, -47.88) * mm, "mid": v(58.44, -44.2) * mm, "end": v(60, -38.83) * mm});
            skArc(sketch, "E79.12", {"start": v(60, 38.83) * mm, "mid": v(58.44, 44.2) * mm, "end": v(54.26, 47.88) * mm});
            skArc(sketch, "E79.13", {"start": v(-60, -38.83) * mm, "mid": v(-58.44, -44.2) * mm, "end": v(-54.26, -47.88) * mm});
            skLineSegment(sketch, "E79.14", {"start": v(-60, 38.83) * mm, "end": v(-60, -38.83) * mm});
            skArc(sketch, "E79.15", {"start": v(-54.26, 47.88) * mm, "mid": v(-58.44, 44.2) * mm, "end": v(-60, 38.83) * mm});
            skCircle(sketch, "E79.16", {"center": v(60, 60) * mm, "radius": 4 * mm});
            skCircle(sketch, "E79.17", {"center": v(-60, 60) * mm, "radius": 4 * mm});
            skCircle(sketch, "E79.18", {"center": v(-60, -60) * mm, "radius": 4 * mm});
            skCircle(sketch, "E79.19", {"center": v(60, -60) * mm, "radius": 4 * mm});
            skLineSegment(sketch, "E80", {"start": v(0, 74.25) * mm, "end": v(0, 102.57) * mm, "construction": true});
            skCircle(sketch, "E81", {"center": v(0, 102.57) * mm, "radius": 6 * mm});
            skLineSegment(sketch, "E82", {"start": v(-32.9, 74.25) * mm, "end": v(-14.9, 92.25) * mm});
            skLineSegment(sketch, "E83", {"start": v(33, 74.25) * mm, "end": v(15, 92.25) * mm});
            skLineSegment(sketch, "E84", {"start": v(-14.9, 92.25) * mm, "end": v(-14.9, 104.25) * mm});
            skLineSegment(sketch, "E85", {"start": v(15, 92.25) * mm, "end": v(15, 102.57) * mm});
            skArc(sketch, "E86", {"start": v(15, 102.57) * mm, "mid": v(0.84, 117.55) * mm, "end": v(-14.9, 104.25) * mm});
            skLineSegment(sketch, "E87", {"start": v(-74.25, 0) * mm, "end": v(74.25, 0) * mm, "construction": true});
            skLineSegment(sketch, "E88.MirrorCS", {"start": v(-32.9, -74.25) * mm, "end": v(-14.9, -92.25) * mm});
            skLineSegment(sketch, "E89.MirrorCS", {"start": v(-14.9, -92.25) * mm, "end": v(-14.9, -104.25) * mm});
            skArc(sketch, "E90.MirrorCS", {"start": v(15, -102.57) * mm, "mid": v(0.84, -117.55) * mm, "end": v(-14.9, -104.25) * mm});
            skLineSegment(sketch, "E91.MirrorCS", {"start": v(15, -92.25) * mm, "end": v(15, -102.57) * mm});
            skLineSegment(sketch, "E92.MirrorCS", {"start": v(33, -74.25) * mm, "end": v(15, -92.25) * mm});
            skCircle(sketch, "E93.MirrorC", {"center": v(0, -102.57) * mm, "radius": 6 * mm});
            skLineSegment(sketch, "E94.MirrorCS", {"start": v(0, -74.25) * mm, "end": v(0, -102.57) * mm, "construction": true});
            skSolve(sketch);
        }
        {
            var Q0;
            Q0 = qSketchRegion(id + "F16", true);
            var Q1;
            Q1=makeQuery(id+"F2.opExtrude","CAP_FACE",FACE,{"disambiguationData":[OSD([sQuery(id+"F0.wireOp",EDGE,"E12"),sQuery(id+"F0.wireOp",EDGE,"E13"),sQuery(id+"F0.wireOp",EDGE,"E14"),sQuery(id+"F0.wireOp",EDGE,"E15"),sQuery(id+"F0.wireOp",EDGE,"E17.filletArc"),sQuery(id+"F0.wireOp",EDGE,"E18.filletArc"),sQuery(id+"F0.wireOp",EDGE,"E19.filletArc"),sQuery(id+"F0.wireOp",EDGE,"E20.filletArc"),sQuery(id+"F0.wireOp",EDGE,"E25.0"),sQuery(id+"F0.wireOp",EDGE,"E25.1"),sQuery(id+"F0.wireOp",EDGE,"E25.2"),sQuery(id+"F0.wireOp",EDGE,"E25.3"),sQuery(id+"F0.wireOp",EDGE,"E25.4"),sQuery(id+"F0.wireOp",EDGE,"E25.5"),sQuery(id+"F0.wireOp",EDGE,"E25.6"),sQuery(id+"F0.wireOp",EDGE,"E25.7")])],"isStart":false});
            extrude(context, id + "F17", {"entities" : qUnion([Q0]), "endBound" : BoundingType.UP_TO_SURFACE, "endBoundEntityFace" : qUnion([Q1]), "depth" : 25 * mm});
        }
    });
